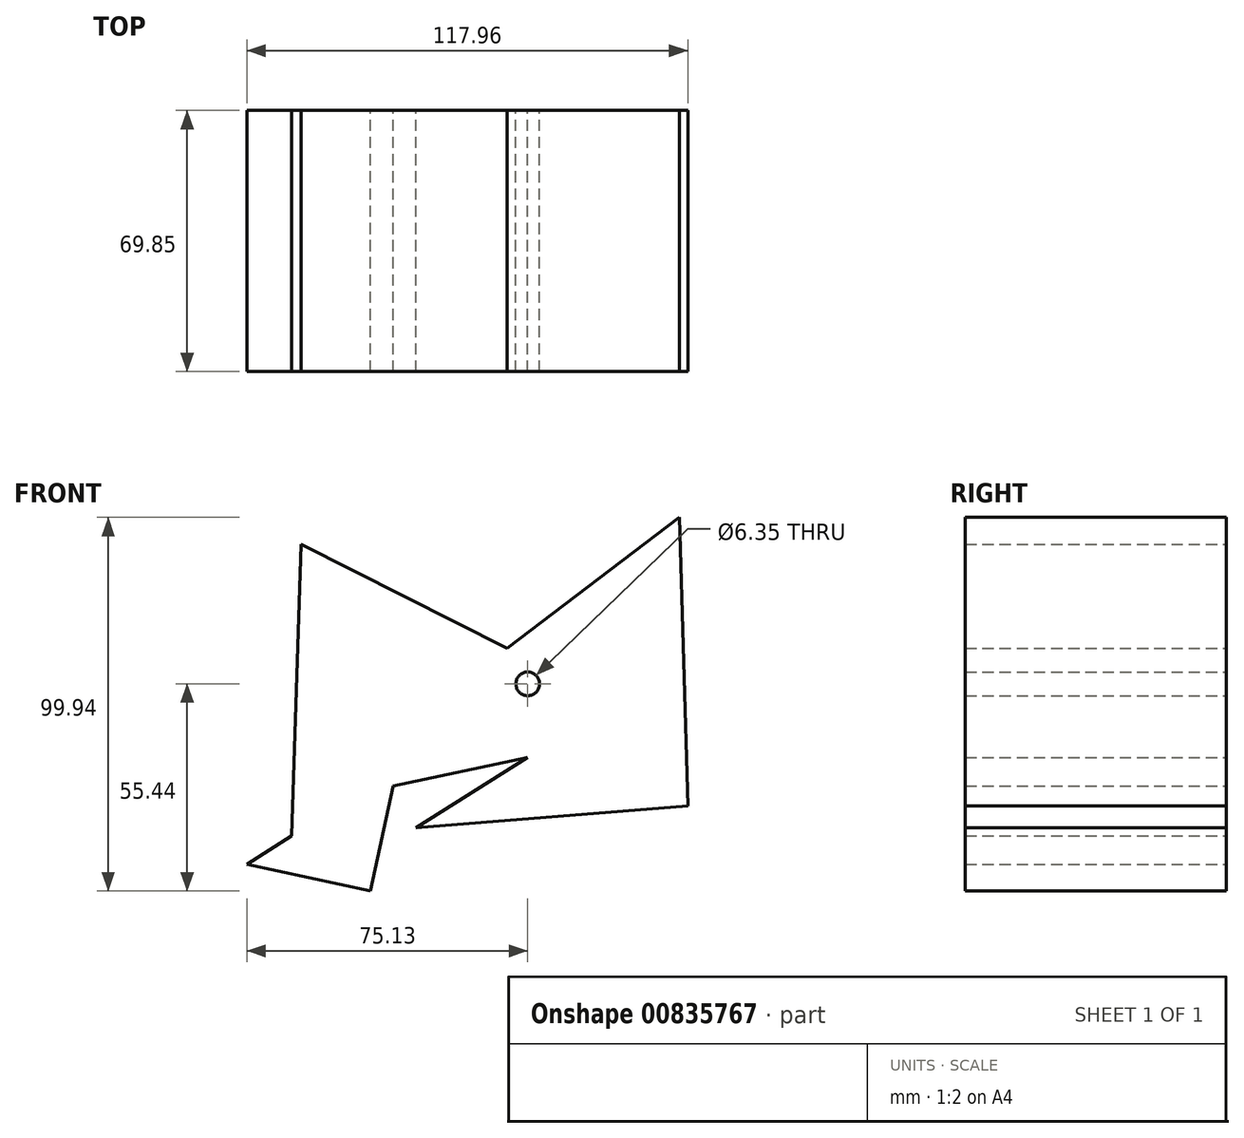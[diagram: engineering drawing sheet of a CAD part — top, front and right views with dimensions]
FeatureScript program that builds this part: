
annotation { "Feature Type Name" : "Feature", "Feature Type Description" : "" }
export const myFeature = defineFeature(function(context is Context, id is Id, definition is map)
    precondition{}
    {
        {
            var Q0;
            Q0=qCreatedBy(makeId("Front.planeOp"),FACE);
            var sketch = newSketch(context, id + "F0", { "sketchPlane" : qUnion([Q0])});
            skLineSegment(sketch, "E0", {"start": v(-63.13, -40.66) * mm, "end": v(-60.66, 37.34) * mm});
            skLineSegment(sketch, "E1", {"start": v(-60.66, 37.34) * mm, "end": v(-5.58, 9.46) * mm});
            skLineSegment(sketch, "E2", {"start": v(-5.58, 9.46) * mm, "end": v(40.64, 44.5) * mm});
            skLineSegment(sketch, "E3", {"start": v(40.64, 44.5) * mm, "end": v(42.83, -32.72) * mm});
            skLineSegment(sketch, "E4", {"start": v(42.83, -32.72) * mm, "end": v(-29.88, -38.56) * mm});
            skLineSegment(sketch, "E5", {"start": v(-29.88, -38.56) * mm, "end": v(0, -19.64) * mm});
            skLineSegment(sketch, "E6", {"start": v(0, -19.64) * mm, "end": v(-35.96, -27.34) * mm});
            skLineSegment(sketch, "E7", {"start": v(-35.96, -27.34) * mm, "end": v(-42.08, -55.44) * mm});
            skLineSegment(sketch, "E8", {"start": v(-42.08, -55.44) * mm, "end": v(-75.13, -48.24) * mm});
            skLineSegment(sketch, "E9", {"start": v(-75.13, -48.24) * mm, "end": v(-63.13, -40.66) * mm});
            skSolve(sketch);
        }
        {
            var Q0;
            Q0=makeQuery(id+"F0.imprint","IMPRINT",FACE,{"disambiguationData":[TD([[makeQuery(id+"F0.imprint","IMPRINT",EDGE,{"derivedFrom":sQuery(id+"F0.wireOp",EDGE,"E0")}),-1.0]])]});
            extrude(context, id + "F1", {"entities" : qUnion([Q0]), "depth" : 69.85 * mm, "offsetDistance" : 25.4 * mm});
        }
        {
            var Q0;
            Q0=makeQuery(id+"F1.opExtrude","CAP_FACE",FACE,{"disambiguationData":[OSD([sQuery(id+"F0.wireOp",EDGE,"E0"),sQuery(id+"F0.wireOp",EDGE,"E1"),sQuery(id+"F0.wireOp",EDGE,"E2"),sQuery(id+"F0.wireOp",EDGE,"E3"),sQuery(id+"F0.wireOp",EDGE,"E4"),sQuery(id+"F0.wireOp",EDGE,"E5"),sQuery(id+"F0.wireOp",EDGE,"E6"),sQuery(id+"F0.wireOp",EDGE,"E7"),sQuery(id+"F0.wireOp",EDGE,"E8"),sQuery(id+"F0.wireOp",EDGE,"E9")])],"isStart":true});
            var sketch = newSketch(context, id + "F2", { "sketchPlane" : qUnion([Q0])});
            skCircle(sketch, "E10", {"center": v(0, 0) * mm, "radius": 9.28 * mm});
            skSolve(sketch);
        }
        {
            var Q0;
            Q0=sQuery(id+"F2.wireOp",VERTEX,"E10.center");
            var Q1;
            Q1=makeQuery(id+"F1.opExtrude","SWEPT_BODY",BODY,{"disambiguationData":[OSD([sQuery(id+"F0.wireOp",EDGE,"E0"),sQuery(id+"F0.wireOp",EDGE,"E1"),sQuery(id+"F0.wireOp",EDGE,"E2"),sQuery(id+"F0.wireOp",EDGE,"E3"),sQuery(id+"F0.wireOp",EDGE,"E4"),sQuery(id+"F0.wireOp",EDGE,"E5"),sQuery(id+"F0.wireOp",EDGE,"E6"),sQuery(id+"F0.wireOp",EDGE,"E7"),sQuery(id+"F0.wireOp",EDGE,"E8"),sQuery(id+"F0.wireOp",EDGE,"E9")])]});
            hole(context, id + "F3", {"style" : HoleStyle.SIMPLE, "endStyle" : HoleEndStyle.THROUGH, "holeDiameter" : 6.35 * mm, "majorDiameter" : 6.35 * mm, "isTappedThrough" : true, "tappedDepth" : 12.7 * mm, "tapClearance" : 3, "locations" : qUnion([Q0]), "scope" : qUnion([Q1])});
        }
    });
